# Revit family: ASH_ArmitageShanks_WCPans_Sandringham21_E8974
name_source: partatom
category: Plumbing Fixtures
revit_build: Autodesk Revit MEP 2012 (Build: 20110309_2315(x64)
units: mm (PartAtom-declared; Revit-internal decimal feet)

## types (1)
- E897401-Sandringham 21 Back To Wall WC Suite
    Accessories = www.idealspec.co.uk
    AreaUnits = millimeters
    Assembly Code = C1030200
    AssetType = Fixed
    BIMObjectName = ASH_ArmitageShanks_WCPans_Sandringham21-BTW_E8974
    Brand = Armitage Shanks
    CWFU = 0
    Color = White
    ConnectionType = Plumbing
    Cost = 0 $
    Default Elevation = 1219 mm
    Description = Sandringham 21 back-to-wall wc pan
    DurationUnit = year
    ECA = No
    ExpectedLife = 30
    Features = back-to-wall wc pan with horizontal outlet
    Finish = White
    HWFU = 0
    Help = www.idealspec.co.uk/contact-us.html
    IfcExportAs = IfcSanitaryTerminalType
    IfcExportType = TOILETPAN
    InstallationInstructions = www.idealspec.co.uk/resources.html
    LinearUnits = millimeters
    ManufacturerURL = www.idealspec.co.uk
    Material = Vitreous china
    Model = E897401
    ModelNumber = E897401
    ModelReference = Sandringham 21 back-to-wall wc pan
    NBSDescription = WC pans
    NBSReference = 45-36-70/384
    Name = WCPans_Sandringham21-BTW-E8974
    NettWeight = 17 KG
    NominalDepth = 520 mm
    NominalHeight = 400 mm
    NominalLength = 520 mm
    NominalWidth = 360 mm
    PanColor = White
    PanMaterial = Vitreous china
    PanMounting = BackToWall
    ProductInformation = www.idealspec.co.uk/assets/datasheet/E897401
    Shape = Sculptured
    Size = 520 x 360 x 400 mm
    Space = Internal
    SpareParts = www.fastpart-spares.co.uk
    SpilloverLevel = 400 mm
    ToiletPanType = WashDown
    ToiletType = Other
    URL = www.idealspec.co.uk
    Uniclass2 = Pr_40_20_93_94
    Version = 2
    VolumeUnits = Litres
    WFU = 0
    WRAS = No
    WarrantyDescription = Manufacturers Warranty
    WarrantyDurationParts = 99
    WarrantyDurationUnit = year
    WaterEfficientProduct = No

## geometry (parser evidence)
native form markers: Sweep x4
no freeform markers — native parametric forms only
